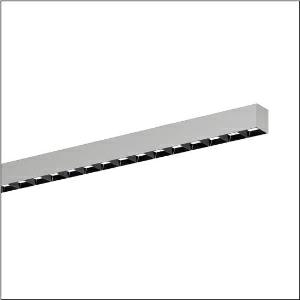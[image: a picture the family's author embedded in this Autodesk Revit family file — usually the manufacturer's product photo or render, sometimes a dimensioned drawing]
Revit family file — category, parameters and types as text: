
# Revit family: silica_r__21_51mx21tat4s_03ed
name_source: partatom
category: Lighting Fixtures
units: mm (PartAtom-declared; Revit-internal decimal feet)

## family parameters
Cut with Voids When Loaded = No
Host = Face
Light Source = No
Part Type = Normal
Room Calculation Point = No
Round Connector Dimension = Use Diameter
Shared = No

## types (1)
- --- (1 x LED, 3720 lm, 32.2 W, 6500K)
    Apparent Load = 32 VA
    CIE Flux Codes = 85 99 100 100 100
    Color Rendering = 80
    Color Temperature = 6500K
    Default Elevation = 1800 mm
    Description = Silica® 21, office luminaire, primary light control with darklight reflector, of PMMA, black, CAT 2 (L<= 3000cd/m²), light emission: direct distribution, primary light characteristic: symmetric, installation type: surface-mounted, LED, rated luminous flux: 3.720lm, luminous efficacy: 110lm/W, light colour: 8tw, colour temperature: 2700..6500K, control gear: ECG DALI, with terminal, 3+2-pole, max. 2.5mm², mains connection: 220..240V, AC, 50/60Hz, rated input power: 33.8W, luminaire housing, of aluminium, metallic grey (RAL 9006), length: 1.204mm, width: 53mm, height: 53mm, protection rating (complete): IP20, insulation class (complete): insulation class I (protective earthing), certification: CE, permissible operating ambient temperature: 0..+35°C, standard: EN 50419, packaging unit: 1 piece
    Height = 0 mm  [stored 0 ft]
    Lamp = 1 x LED
    Lamp Light Flux = 3720 lm
    Lamp Power = 32.2 W
    Lamp count = 1
    Length = 1204 mm
    Luminous efficacy = 116 lm/W
    Manufacturer = Siteco
    ModVariant = No
    Model = 51MX21TAT4S
    Mounting Place = Ceiling
    Mounting Type = Recessed
    Number of Poles = 1
    OnlyDefault = Yes
    Power Factor = 1
    Product Name = Silica® 21
    Product group = office luminaire | ceiling recessed
    ProductGroupID = 400
    Protection Class = Protection class I
    Protection Degree = IP 20
    RLX_Detail_Level = 1
    RLX_Emergency_Light_Flux = 0 lm
    RLX_Emergency_Type = 0
    RLX_Emergency_Type_DB = No
    RlxData = <blob elided: 39341 chars, md5=98bbc622>
    Socket = socket
    Standby Power = 0 W
    System Light Flux = 3720 lm
    System Power = 32 W
    Type Comments = individual setting
    Type Image = l_1335929.jpg
    URL = http://relux.com
    VarID = @adj_109855
    Voltage = 0 V
    Weight = 0.00 kg
    Width = 53 mm

note: [stored X ft] marks values corroborated as IEEE doubles in the binary element streams (Revit-internal decimal feet)

## geometry (parser evidence)
native form markers: Blend x4, Sweep x10
no freeform markers — native parametric forms only
